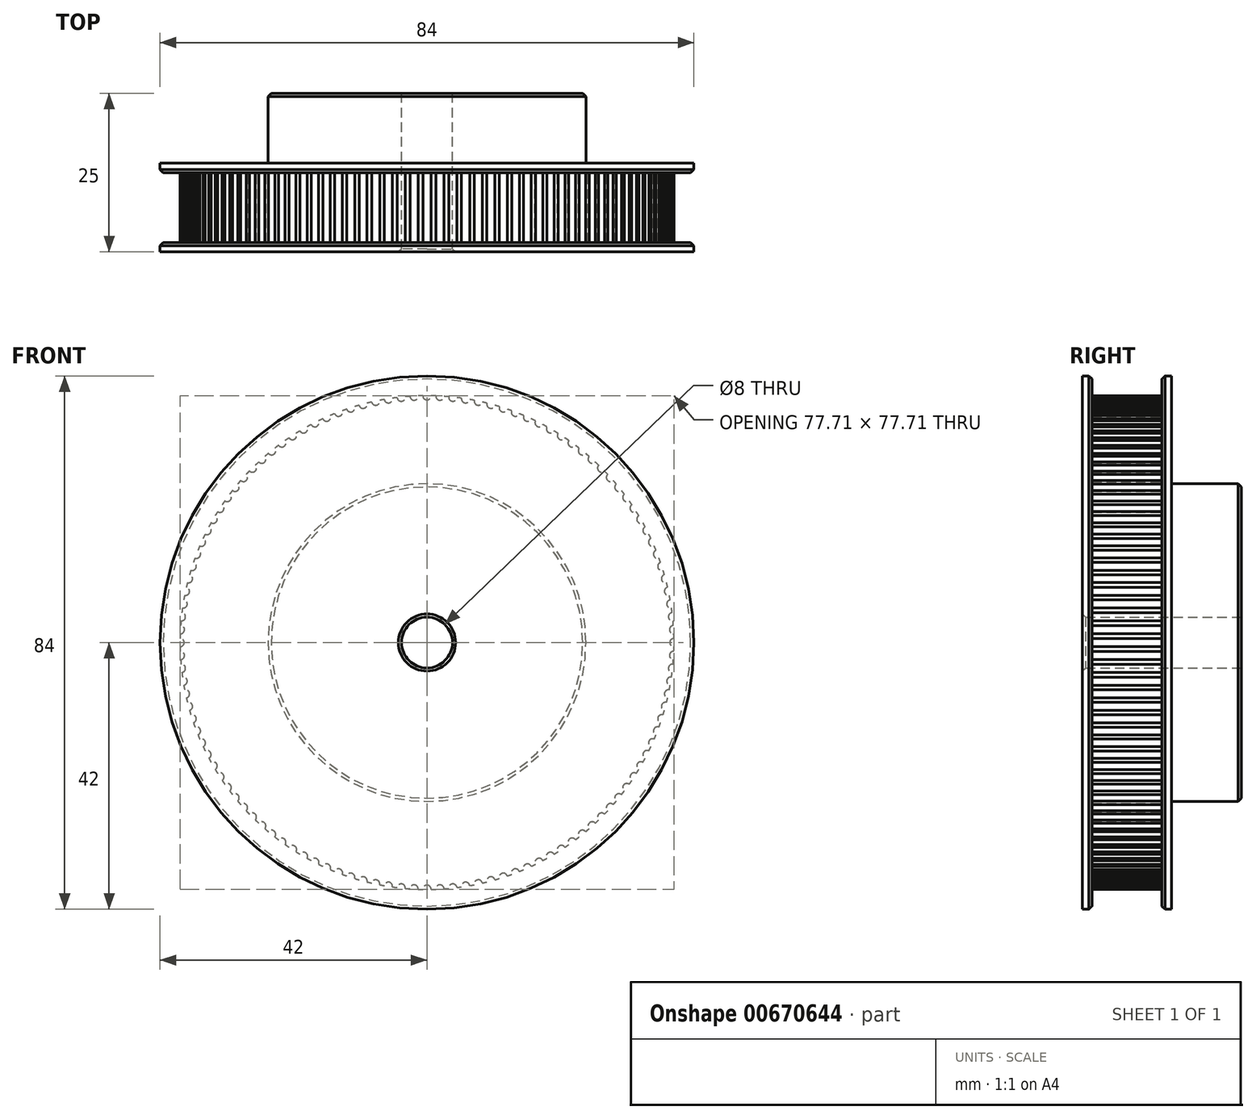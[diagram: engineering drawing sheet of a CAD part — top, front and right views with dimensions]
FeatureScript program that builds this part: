
annotation { "Feature Type Name" : "Feature", "Feature Type Description" : "" }
export const myFeature = defineFeature(function(context is Context, id is Id, definition is map)
    precondition{}
    {
        {
            var Q0;
            Q0=qCreatedBy(makeId("Front.planeOp"),FACE);
            var sketch = newSketch(context, id + "F0", { "sketchPlane" : qUnion([Q0])});
            skCircle(sketch, "E0", {"center": v(0, 0) * mm, "radius": 38.86 * mm});
            skSolve(sketch);
        }
        {
            var Q0;
            Q0=makeQuery(id+"F0.imprint","IMPRINT",FACE,{"disambiguationData":[TD([[makeQuery(id+"F0.imprint","IMPRINT",EDGE,{"derivedFrom":sQuery(id+"F0.wireOp",EDGE,"E0")}),1.0]])]});
            extrude(context, id + "F1", {"entities" : qUnion([Q0]), "endBound" : BoundingType.SYMMETRIC, "depth" : 11 * mm, "offsetDistance" : 25 * mm});
        }
        {
            var Q0;
            Q0=makeQuery(id+"F1.opExtrude","CAP_FACE",FACE,{"disambiguationData":[OSD([sQuery(id+"F0.wireOp",EDGE,"E0")])],"isStart":false});
            var sketch = newSketch(context, id + "F2", { "sketchPlane" : qUnion([Q0])});
            skCircle(sketch, "E1", {"center": v(0, 0) * mm, "radius": 42 * mm});
            skSolve(sketch);
        }
        {
            var Q0;
            Q0=qSketchRegion(id+"F2",true);
            extrude(context, id + "F3", {"entities" : qUnion([Q0]), "operationType" : NewBodyOperationType.ADD, "depth" : 1.5 * mm, "offsetDistance" : 25 * mm});
        }
        {
            var Q0;
            Q0=makeQuery(id+"F1.opExtrude","CAP_FACE",FACE,{"disambiguationData":[OSD([sQuery(id+"F0.wireOp",EDGE,"E0")])],"isStart":true});
            var sketch = newSketch(context, id + "F4", { "sketchPlane" : qUnion([Q0])});
            skCircle(sketch, "E2", {"center": v(0, 0) * mm, "radius": 42 * mm});
            skSolve(sketch);
        }
        {
            var Q0;
            Q0=qSketchRegion(id+"F4",true);
            extrude(context, id + "F5", {"entities" : qUnion([Q0]), "operationType" : NewBodyOperationType.ADD, "depth" : 1.5 * mm, "offsetDistance" : 25 * mm});
        }
        {
            var Q0;
            Q0=makeQuery(id+"F5.opExtrude","CAP_FACE",FACE,{"disambiguationData":[OSD([sQuery(id+"F4.wireOp",EDGE,"E2")])],"isStart":false});
            var sketch = newSketch(context, id + "F6", { "sketchPlane" : qUnion([Q0])});
            skCircle(sketch, "E3", {"center": v(0, 0) * mm, "radius": 25 * mm});
            skSolve(sketch);
        }
        {
            var Q0;
            Q0=qSketchRegion(id+"F6",true);
            extrude(context, id + "F7", {"entities" : qUnion([Q0]), "operationType" : NewBodyOperationType.ADD, "depth" : 11 * mm, "offsetDistance" : 25 * mm});
        }
        {
            var Q0;
            Q0=makeQuery(id+"F7.opExtrude","CAP_FACE",FACE,{"disambiguationData":[OSD([sQuery(id+"F6.wireOp",EDGE,"E3")])],"isStart":false});
            var sketch = newSketch(context, id + "F8", { "sketchPlane" : qUnion([Q0])});
            skCircle(sketch, "E4", {"center": v(0, 0) * mm, "radius": 4 * mm});
            skSolve(sketch);
        }
        {
            var Q0;
            Q0=qSketchRegion(id+"F8",true);
            extrude(context, id + "F9", {"entities" : qUnion([Q0]), "operationType" : NewBodyOperationType.REMOVE, "endBound" : BoundingType.THROUGH_ALL, "oppositeDirection" : true, "depth" : 25 * mm, "offsetDistance" : 25 * mm});
        }
        {
            var Q0;
            Q0=makeQuery(id+"F9.boolean.opBoolean","INTERSECT",EDGE,{"derivedFrom":[makeQuery(id+"F3.opExtrude","CAP_FACE",FACE,{"disambiguationData":[OSD([sQuery(id+"F2.wireOp",EDGE,"E1")])],"isStart":false}),makeQuery(id+"F9.opExtrude","SWEPT_FACE",FACE,{"disambiguationData":[OSD([sQuery(id+"F8.wireOp",EDGE,"E4")])]})]});
            var Q1;
            Q1=makeQuery(id+"F9.boolean.opBoolean","COPY",EDGE,{"derivedFrom":makeQuery(id+"F9.opExtrude","CAP_EDGE",EDGE,{"disambiguationData":[OSD([sQuery(id+"F8.wireOp",EDGE,"E4")])],"isStart":true})});
            var Q2;
            Q2=makeQuery(id+"F3.opExtrude","CAP_EDGE",EDGE,{"disambiguationData":[OSD([sQuery(id+"F2.wireOp",EDGE,"E1")])],"isStart":true});
            var Q3;
            Q3=makeQuery(id+"F5.opExtrude","CAP_EDGE",EDGE,{"disambiguationData":[OSD([sQuery(id+"F4.wireOp",EDGE,"E2")])],"isStart":true});
            var Q4;
            Q4=makeQuery(id+"F7.opExtrude","CAP_EDGE",EDGE,{"disambiguationData":[OSD([sQuery(id+"F6.wireOp",EDGE,"E3")])],"isStart":false});
            chamfer(context, id + "F10", {"entities" : qUnion([Q0, Q1, Q2, Q3, Q4]), "width" : 0.5 * mm, "tangentPropagation" : true});
        }
        {
            var Q0;
            Q0=makeQuery(id+"F5.opExtrude","CAP_FACE",FACE,{"disambiguationData":[OSD([sQuery(id+"F4.wireOp",EDGE,"E2")])],"isStart":true});
            var sketch = newSketch(context, id + "F11", { "sketchPlane" : qUnion([Q0])});
            skCircle(sketch, "E5", {"center": v(0, 0) * mm, "radius": 38.86 * mm, "construction": true});
            skLineSegment(sketch, "E6", {"start": v(0, 0) * mm, "end": v(0, -38.86) * mm, "construction": true});
            skCircle(sketch, "E7", {"center": v(0, -38.86) * mm, "radius": 0.65 * mm});
            skCircle(sketch, "E8.1.0", {"center": v(2.03, -38.8) * mm, "radius": 0.65 * mm});
            skCircle(sketch, "E8.2.0", {"center": v(4.06, -38.65) * mm, "radius": 0.65 * mm});
            skCircle(sketch, "E8.3.0", {"center": v(6.08, -38.38) * mm, "radius": 0.65 * mm});
            skCircle(sketch, "E8.4.0", {"center": v(8.08, -38.01) * mm, "radius": 0.65 * mm});
            skCircle(sketch, "E8.5.0", {"center": v(10.06, -37.54) * mm, "radius": 0.65 * mm});
            skCircle(sketch, "E8.6.0", {"center": v(12, -36.96) * mm, "radius": 0.65 * mm});
            skCircle(sketch, "E8.7.0", {"center": v(13.93, -36.28) * mm, "radius": 0.65 * mm});
            skCircle(sketch, "E8.8.0", {"center": v(15.8, -35.5) * mm, "radius": 0.65 * mm});
            skCircle(sketch, "E8.9.0", {"center": v(17.64, -34.62) * mm, "radius": 0.65 * mm});
            skCircle(sketch, "E8.10.0", {"center": v(19.43, -33.65) * mm, "radius": 0.65 * mm});
            skCircle(sketch, "E8.11.0", {"center": v(21.16, -32.6) * mm, "radius": 0.65 * mm});
            skCircle(sketch, "E8.12.0", {"center": v(22.84, -31.44) * mm, "radius": 0.65 * mm});
            skCircle(sketch, "E8.13.0", {"center": v(24.46, -30.2) * mm, "radius": 0.65 * mm});
            skCircle(sketch, "E8.14.0", {"center": v(26, -28.88) * mm, "radius": 0.65 * mm});
            skCircle(sketch, "E8.15.0", {"center": v(27.48, -27.48) * mm, "radius": 0.65 * mm});
            skCircle(sketch, "E8.16.0", {"center": v(28.88, -26) * mm, "radius": 0.65 * mm});
            skCircle(sketch, "E8.17.0", {"center": v(30.2, -24.46) * mm, "radius": 0.65 * mm});
            skCircle(sketch, "E8.18.0", {"center": v(31.44, -22.84) * mm, "radius": 0.65 * mm});
            skCircle(sketch, "E8.19.0", {"center": v(32.6, -21.16) * mm, "radius": 0.65 * mm});
            skCircle(sketch, "E8.20.0", {"center": v(33.65, -19.43) * mm, "radius": 0.65 * mm});
            skCircle(sketch, "E8.21.0", {"center": v(34.62, -17.64) * mm, "radius": 0.65 * mm});
            skCircle(sketch, "E8.22.0", {"center": v(35.5, -15.8) * mm, "radius": 0.65 * mm});
            skCircle(sketch, "E8.23.0", {"center": v(36.28, -13.93) * mm, "radius": 0.65 * mm});
            skCircle(sketch, "E8.24.0", {"center": v(36.96, -12) * mm, "radius": 0.65 * mm});
            skCircle(sketch, "E8.25.0", {"center": v(37.54, -10.06) * mm, "radius": 0.65 * mm});
            skCircle(sketch, "E8.26.0", {"center": v(38.01, -8.08) * mm, "radius": 0.65 * mm});
            skCircle(sketch, "E8.27.0", {"center": v(38.38, -6.08) * mm, "radius": 0.65 * mm});
            skCircle(sketch, "E8.28.0", {"center": v(38.65, -4.06) * mm, "radius": 0.65 * mm});
            skCircle(sketch, "E8.29.0", {"center": v(38.8, -2.03) * mm, "radius": 0.65 * mm});
            skCircle(sketch, "E8.30.0", {"center": v(38.86, 0) * mm, "radius": 0.65 * mm});
            skCircle(sketch, "E8.31.0", {"center": v(38.8, 2.03) * mm, "radius": 0.65 * mm});
            skCircle(sketch, "E8.32.0", {"center": v(38.65, 4.06) * mm, "radius": 0.65 * mm});
            skCircle(sketch, "E8.33.0", {"center": v(38.38, 6.08) * mm, "radius": 0.65 * mm});
            skCircle(sketch, "E8.34.0", {"center": v(38.01, 8.08) * mm, "radius": 0.65 * mm});
            skCircle(sketch, "E8.35.0", {"center": v(37.54, 10.06) * mm, "radius": 0.65 * mm});
            skCircle(sketch, "E8.36.0", {"center": v(36.96, 12) * mm, "radius": 0.65 * mm});
            skCircle(sketch, "E8.37.0", {"center": v(36.28, 13.93) * mm, "radius": 0.65 * mm});
            skCircle(sketch, "E8.38.0", {"center": v(35.5, 15.8) * mm, "radius": 0.65 * mm});
            skCircle(sketch, "E8.39.0", {"center": v(34.62, 17.64) * mm, "radius": 0.65 * mm});
            skCircle(sketch, "E8.40.0", {"center": v(33.65, 19.43) * mm, "radius": 0.65 * mm});
            skCircle(sketch, "E8.41.0", {"center": v(32.6, 21.16) * mm, "radius": 0.65 * mm});
            skCircle(sketch, "E8.42.0", {"center": v(31.44, 22.84) * mm, "radius": 0.65 * mm});
            skCircle(sketch, "E8.43.0", {"center": v(30.2, 24.46) * mm, "radius": 0.65 * mm});
            skCircle(sketch, "E8.44.0", {"center": v(28.88, 26) * mm, "radius": 0.65 * mm});
            skCircle(sketch, "E8.45.0", {"center": v(27.48, 27.48) * mm, "radius": 0.65 * mm});
            skCircle(sketch, "E8.46.0", {"center": v(26, 28.88) * mm, "radius": 0.65 * mm});
            skCircle(sketch, "E8.47.0", {"center": v(24.46, 30.2) * mm, "radius": 0.65 * mm});
            skCircle(sketch, "E8.48.0", {"center": v(22.84, 31.44) * mm, "radius": 0.65 * mm});
            skCircle(sketch, "E8.49.0", {"center": v(21.16, 32.6) * mm, "radius": 0.65 * mm});
            skCircle(sketch, "E8.50.0", {"center": v(19.43, 33.65) * mm, "radius": 0.65 * mm});
            skCircle(sketch, "E8.51.0", {"center": v(17.64, 34.62) * mm, "radius": 0.65 * mm});
            skCircle(sketch, "E8.52.0", {"center": v(15.8, 35.5) * mm, "radius": 0.65 * mm});
            skCircle(sketch, "E8.53.0", {"center": v(13.93, 36.28) * mm, "radius": 0.65 * mm});
            skCircle(sketch, "E8.54.0", {"center": v(12, 36.96) * mm, "radius": 0.65 * mm});
            skCircle(sketch, "E8.55.0", {"center": v(10.06, 37.54) * mm, "radius": 0.65 * mm});
            skCircle(sketch, "E8.56.0", {"center": v(8.08, 38.01) * mm, "radius": 0.65 * mm});
            skCircle(sketch, "E8.57.0", {"center": v(6.08, 38.38) * mm, "radius": 0.65 * mm});
            skCircle(sketch, "E8.58.0", {"center": v(4.06, 38.65) * mm, "radius": 0.65 * mm});
            skCircle(sketch, "E8.59.0", {"center": v(2.03, 38.8) * mm, "radius": 0.65 * mm});
            skCircle(sketch, "E8.60.0", {"center": v(0, 38.86) * mm, "radius": 0.65 * mm});
            skCircle(sketch, "E8.61.0", {"center": v(-2.03, 38.8) * mm, "radius": 0.65 * mm});
            skCircle(sketch, "E8.62.0", {"center": v(-4.06, 38.65) * mm, "radius": 0.65 * mm});
            skCircle(sketch, "E8.63.0", {"center": v(-6.08, 38.38) * mm, "radius": 0.65 * mm});
            skCircle(sketch, "E8.64.0", {"center": v(-8.08, 38.01) * mm, "radius": 0.65 * mm});
            skCircle(sketch, "E8.65.0", {"center": v(-10.06, 37.54) * mm, "radius": 0.65 * mm});
            skCircle(sketch, "E8.66.0", {"center": v(-12, 36.96) * mm, "radius": 0.65 * mm});
            skCircle(sketch, "E8.67.0", {"center": v(-13.93, 36.28) * mm, "radius": 0.65 * mm});
            skCircle(sketch, "E8.68.0", {"center": v(-15.8, 35.5) * mm, "radius": 0.65 * mm});
            skCircle(sketch, "E8.69.0", {"center": v(-17.64, 34.62) * mm, "radius": 0.65 * mm});
            skCircle(sketch, "E8.70.0", {"center": v(-19.43, 33.65) * mm, "radius": 0.65 * mm});
            skCircle(sketch, "E8.71.0", {"center": v(-21.16, 32.6) * mm, "radius": 0.65 * mm});
            skCircle(sketch, "E8.72.0", {"center": v(-22.84, 31.44) * mm, "radius": 0.65 * mm});
            skCircle(sketch, "E8.73.0", {"center": v(-24.46, 30.2) * mm, "radius": 0.65 * mm});
            skCircle(sketch, "E8.74.0", {"center": v(-26, 28.88) * mm, "radius": 0.65 * mm});
            skCircle(sketch, "E8.75.0", {"center": v(-27.48, 27.48) * mm, "radius": 0.65 * mm});
            skCircle(sketch, "E8.76.0", {"center": v(-28.88, 26) * mm, "radius": 0.65 * mm});
            skCircle(sketch, "E8.77.0", {"center": v(-30.2, 24.46) * mm, "radius": 0.65 * mm});
            skCircle(sketch, "E8.78.0", {"center": v(-31.44, 22.84) * mm, "radius": 0.65 * mm});
            skCircle(sketch, "E8.79.0", {"center": v(-32.6, 21.16) * mm, "radius": 0.65 * mm});
            skCircle(sketch, "E8.80.0", {"center": v(-33.65, 19.43) * mm, "radius": 0.65 * mm});
            skCircle(sketch, "E8.81.0", {"center": v(-34.62, 17.64) * mm, "radius": 0.65 * mm});
            skCircle(sketch, "E8.82.0", {"center": v(-35.5, 15.8) * mm, "radius": 0.65 * mm});
            skCircle(sketch, "E8.83.0", {"center": v(-36.28, 13.93) * mm, "radius": 0.65 * mm});
            skCircle(sketch, "E8.84.0", {"center": v(-36.96, 12) * mm, "radius": 0.65 * mm});
            skCircle(sketch, "E8.85.0", {"center": v(-37.54, 10.06) * mm, "radius": 0.65 * mm});
            skCircle(sketch, "E8.86.0", {"center": v(-38.01, 8.08) * mm, "radius": 0.65 * mm});
            skCircle(sketch, "E8.87.0", {"center": v(-38.38, 6.08) * mm, "radius": 0.65 * mm});
            skCircle(sketch, "E8.88.0", {"center": v(-38.65, 4.06) * mm, "radius": 0.65 * mm});
            skCircle(sketch, "E8.89.0", {"center": v(-38.8, 2.03) * mm, "radius": 0.65 * mm});
            skCircle(sketch, "E8.90.0", {"center": v(-38.86, 0) * mm, "radius": 0.65 * mm});
            skCircle(sketch, "E8.91.0", {"center": v(-38.8, -2.03) * mm, "radius": 0.65 * mm});
            skCircle(sketch, "E8.92.0", {"center": v(-38.65, -4.06) * mm, "radius": 0.65 * mm});
            skCircle(sketch, "E8.93.0", {"center": v(-38.38, -6.08) * mm, "radius": 0.65 * mm});
            skCircle(sketch, "E8.94.0", {"center": v(-38.01, -8.08) * mm, "radius": 0.65 * mm});
            skCircle(sketch, "E8.95.0", {"center": v(-37.54, -10.06) * mm, "radius": 0.65 * mm});
            skCircle(sketch, "E8.96.0", {"center": v(-36.96, -12) * mm, "radius": 0.65 * mm});
            skCircle(sketch, "E8.97.0", {"center": v(-36.28, -13.93) * mm, "radius": 0.65 * mm});
            skCircle(sketch, "E8.98.0", {"center": v(-35.5, -15.8) * mm, "radius": 0.65 * mm});
            skCircle(sketch, "E8.99.0", {"center": v(-34.62, -17.64) * mm, "radius": 0.65 * mm});
            skCircle(sketch, "E8.100.0", {"center": v(-33.65, -19.43) * mm, "radius": 0.65 * mm});
            skCircle(sketch, "E8.101.0", {"center": v(-32.6, -21.16) * mm, "radius": 0.65 * mm});
            skCircle(sketch, "E8.102.0", {"center": v(-31.44, -22.84) * mm, "radius": 0.65 * mm});
            skCircle(sketch, "E8.103.0", {"center": v(-30.2, -24.46) * mm, "radius": 0.65 * mm});
            skCircle(sketch, "E8.104.0", {"center": v(-28.88, -26) * mm, "radius": 0.65 * mm});
            skCircle(sketch, "E8.105.0", {"center": v(-27.48, -27.48) * mm, "radius": 0.65 * mm});
            skCircle(sketch, "E8.106.0", {"center": v(-26, -28.88) * mm, "radius": 0.65 * mm});
            skCircle(sketch, "E8.107.0", {"center": v(-24.46, -30.2) * mm, "radius": 0.65 * mm});
            skCircle(sketch, "E8.108.0", {"center": v(-22.84, -31.44) * mm, "radius": 0.65 * mm});
            skCircle(sketch, "E8.109.0", {"center": v(-21.16, -32.6) * mm, "radius": 0.65 * mm});
            skCircle(sketch, "E8.110.0", {"center": v(-19.43, -33.65) * mm, "radius": 0.65 * mm});
            skCircle(sketch, "E8.111.0", {"center": v(-17.64, -34.62) * mm, "radius": 0.65 * mm});
            skCircle(sketch, "E8.112.0", {"center": v(-15.8, -35.5) * mm, "radius": 0.65 * mm});
            skCircle(sketch, "E8.113.0", {"center": v(-13.93, -36.28) * mm, "radius": 0.65 * mm});
            skCircle(sketch, "E8.114.0", {"center": v(-12, -36.96) * mm, "radius": 0.65 * mm});
            skCircle(sketch, "E8.115.0", {"center": v(-10.06, -37.54) * mm, "radius": 0.65 * mm});
            skCircle(sketch, "E8.116.0", {"center": v(-8.08, -38.01) * mm, "radius": 0.65 * mm});
            skCircle(sketch, "E8.117.0", {"center": v(-6.08, -38.38) * mm, "radius": 0.65 * mm});
            skCircle(sketch, "E8.118.0", {"center": v(-4.06, -38.65) * mm, "radius": 0.65 * mm});
            skCircle(sketch, "E8.119.0", {"center": v(-2.03, -38.8) * mm, "radius": 0.65 * mm});
            skSolve(sketch);
        }
        {
            var Q0;
            Q0 = qSketchRegion(id + "F11", true);
            var Q1;
            Q1=makeQuery(id+"F3.opExtrude","CAP_FACE",FACE,{"disambiguationData":[OSD([sQuery(id+"F2.wireOp",EDGE,"E1")])],"isStart":true});
            extrude(context, id + "F12", {"entities" : qUnion([Q0]), "operationType" : NewBodyOperationType.REMOVE, "endBound" : BoundingType.UP_TO_SURFACE, "depth" : 25 * mm, "endBoundEntityFace" : qUnion([Q1]), "offsetDistance" : 25 * mm});
        }
    });
